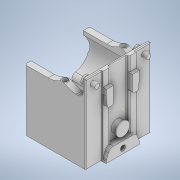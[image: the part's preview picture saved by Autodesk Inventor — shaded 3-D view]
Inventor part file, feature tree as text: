
AUTODESK INVENTOR PART (.ipt)
format: ipt  version: 2022 (Build 260153000, 153)  size: 810,496 bytes
history: native  units: mm
features: reference x24, sketch x23, extrude x21, projected_geometry x19, other x11, fillet x11, chamfer x1
ambient origin geometry x8: Origin, YZ Plane, XZ Plane, XY Plane, X Axis, Y Axis, Z Axis, Center Point
bodies: Body1 (feature_tree)
feature tree (110):
  other  "Твердое тело1"
  extrude  "Выдавливание1"  Depth=34.5mm TaperAngle=0.0deg
  extrude  "Выдавливание2"  Depth=0.5mm
  extrude  "Выдавливание3"  Depth=0.3mm
  extrude  "Выдавливание4"  Depth=5.0mm
  extrude  "Выдавливание5"  Depth=5.0mm
  extrude  "Выдавливание6"  Depth=5.0mm
  extrude  "Выдавливание8"  Depth=15.0mm
  extrude  "Выдавливание9"  Depth=15.0mm
  chamfer  "Фаска1"  Distance=15.0mm
  fillet  "Сопряжение1"  Radius=1.7mm
  extrude  "Выдавливание11"  Depth=2.0mm TaperAngle=0.0deg
  fillet  "Сопряжение4"  Radius=0.8mm
  fillet  "Сопряжение5"  Radius=4.7mm
  sketch  "Эскиз15"
  extrude  "Выдавливание12"  Depth=0.4mm
  sketch  "Эскиз17"
  extrude  "Выдавливание13"  Depth=0.4mm
  extrude  "Выдавливание18"  Depth=200.0mm TaperAngle=0.0deg
  extrude  "Выдавливание19"  Depth=0.5mm TaperAngle=0.0deg
  extrude  "Выдавливание20"  Depth=2.3mm TaperAngle=0.0deg
  extrude  "Выдавливание21"  Depth=10.0mm
  fillet  "Сопряжение13"  Radius=10.0mm
  fillet  "Сопряжение14"  Radius=3.0mm
  fillet  "Сопряжение15"  Radius=4.0mm
  extrude  "Выдавливание22"  Depth=3.0mm
  fillet  "Сопряжение16"  Radius=4.0mm
  extrude  "Выдавливание23"  Depth=2.3mm TaperAngle=0.0deg
  extrude  "Выдавливание24"  Depth=2.0mm TaperAngle=45.0deg
  fillet  "Сопряжение17"  Radius=10.0mm
  extrude  "Выдавливание25"  Depth=30.0mm
  fillet  "Сопряжение19"  Radius=0.8mm
  extrude  "Выдавливание26"  Depth=0.15mm
  fillet  "Сопряжение20"  Radius=3.0mm
  extrude  "Выдавливание27"  Depth=50.0mm TaperAngle=0.0deg
  fillet  "Сопряжение21"  Radius=4.0mm
  sketch  "Эскиз1"
  reference  "Ссылка1"
  reference  "Ссылка2"
  reference  "Ссылка3"
  reference  "Ссылка4"
  reference  "Ссылка5"
  reference  "Ссылка6"
  reference  "Ссылка7"
  reference  "Ссылка8"
  sketch  "Эскиз2"
  projected_geometry  "Спроецированная петля1"
  projected_geometry  "Спроецированная петля2"
  sketch  "Эскиз3"
  reference  "Ссылка9"
  reference  "Ссылка10"
  sketch  "Эскиз4"
  projected_geometry  "Спроецированная петля3"
  reference  "Ссылка11"
  reference  "Ссылка12"
  reference  "Ссылка13"
  reference  "Ссылка14"
  sketch  "Эскиз5"
  reference  "Ссылка15"
  reference  "Ссылка16"
  projected_geometry  "Спроецированная петля4"
  sketch  "Эскиз7"
  projected_geometry  "Спроецированная петля6"
  sketch  "Эскиз11"
  projected_geometry  "Спроецированная петля8"
  sketch  "Эскиз12"
  reference  "Ссылка27"
  sketch  "Эскиз14"
  sketch  "Эскиз16"
  reference  "Ссылка29"
  projected_geometry  "Спроецированная петля10"
  projected_geometry  "Спроецированная петля11"
  projected_geometry  "Спроецированная петля12"
  reference  "Ссылка30"
  reference  "Ссылка31"
  sketch  "Эскиз18"
  projected_geometry  "Спроецированная петля14"
  sketch  "Эскиз23"
  projected_geometry  "Спроецированная петля23"
  sketch  "Эскиз24"
  projected_geometry  "Спроецированная петля24"
  sketch  "Эскиз25"
  sketch  "Эскиз26"
  sketch  "Эскиз27"
  projected_geometry  "Спроецированная петля25"
  sketch  "Эскиз28"
  sketch  "Эскиз29"
  sketch  "Эскиз30"
  reference  "Ссылка32"
  projected_geometry  "Спроецированная петля26"
  projected_geometry  "Спроецированная петля27"
  reference  "Ссылка33"
  projected_geometry  "Спроецированная петля28"
  sketch  "Эскиз31"
  projected_geometry  "Спроецированная петля29"
  projected_geometry  "Спроецированная петля30"
  reference  "Ссылка34"
  reference  "Ссылка35"
  sketch  "Эскиз32"
  projected_geometry  "Спроецированная петля31"
  other  "<userpath>\OneDrive\Документы\Git\MZCAT_battery\FastBattery.iam"
  other  "FastBattery.iam"
  other  "plan:1"
  other  "BMS_board:1"
  other  "metal_body:1"
  other  "metal_cap:1"
  other  "<userpath>\Documents\Git\MZCAT_battery\FastBattery2.iam"
  other  "FastBattery2.iam"
  other  "metal_body_fixed:1"
  other  "<userpath>\Documents\Git\MZCAT_2024_construction\MZCAT_battery\FastBattery2.iam"
